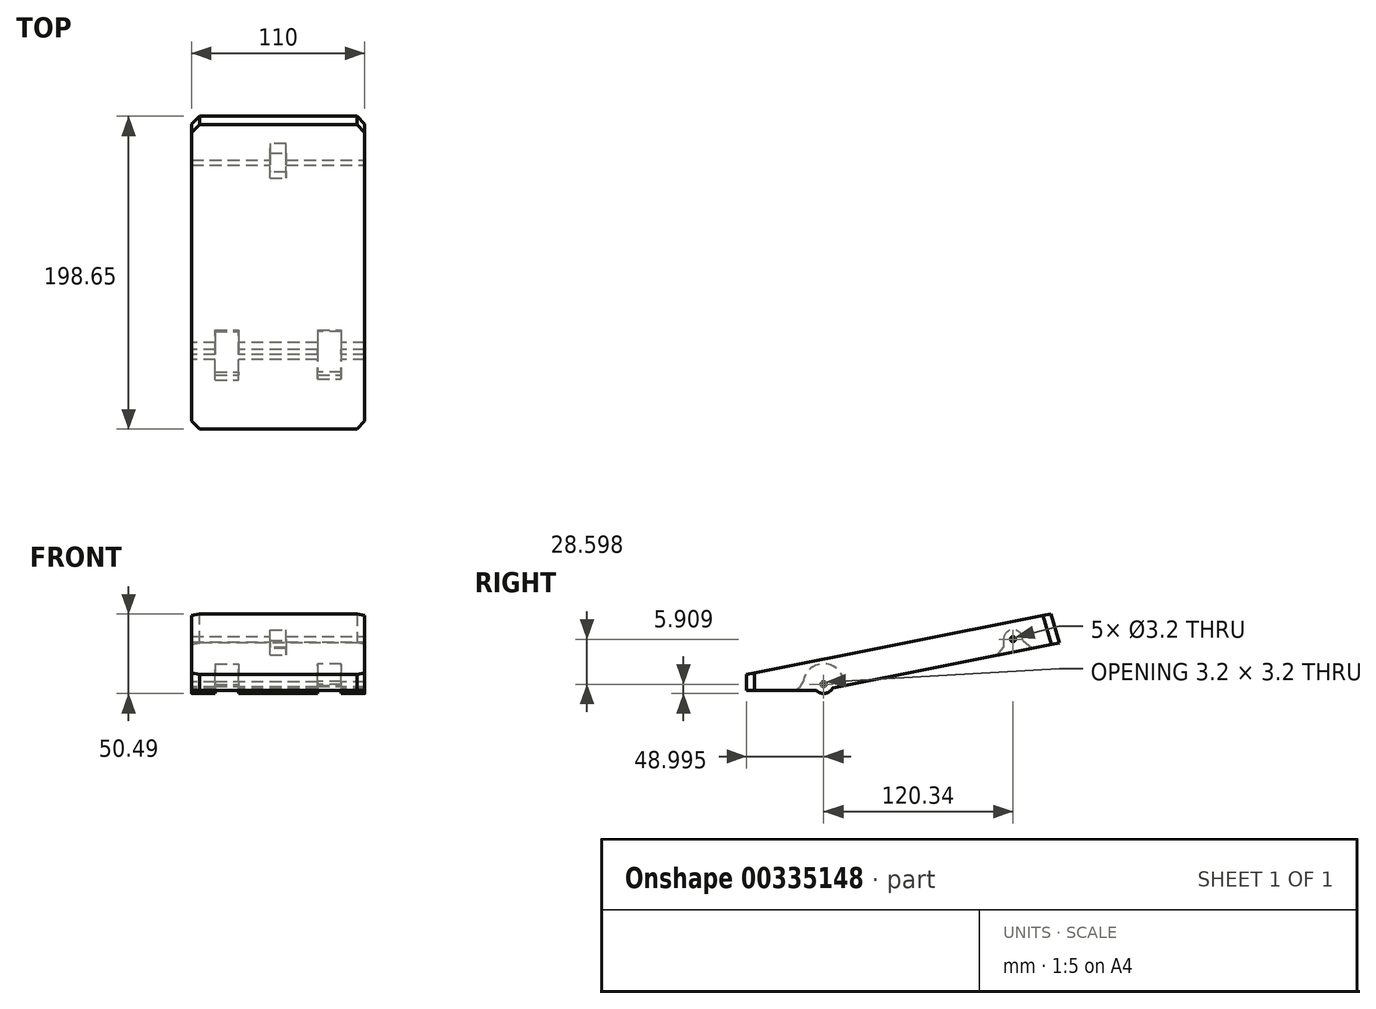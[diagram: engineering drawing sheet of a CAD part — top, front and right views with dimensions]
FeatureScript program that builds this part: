
annotation { "Feature Type Name" : "Feature", "Feature Type Description" : "" }
export const myFeature = defineFeature(function(context is Context, id is Id, definition is map)
    precondition{}
    {
        {
            var Q0;
            Q0=qCreatedBy(makeId("Right.planeOp"),FACE);
            cPlane(context, id + "F0", {"entities" : qUnion([Q0]), "cplaneType" : CPlaneType.OFFSET, "offset" : 55 * mm, "width" : 150 * mm, "height" : 150 * mm});
        }
        {
            var Q0;
            Q0=qCreatedBy(makeId("Right.planeOp"),FACE);
            var sketch = newSketch(context, id + "F1", { "sketchPlane" : qUnion([Q0])});
            skCircle(sketch, "E0.0", {"center": v(-48.56, 3.8) * mm, "radius": 1.6 * mm});
            skArc(sketch, "E1", {"start": v(-53.35, 0) * mm, "mid": v(-47.61, -2.03) * mm, "end": v(-42.71, 1.57) * mm});
            skLineSegment(sketch, "E2", {"start": v(-42.71, 1.57) * mm, "end": v(101.09, 30.13) * mm});
            skLineSegment(sketch, "E3", {"start": v(-97.56, 0) * mm, "end": v(-97.56, 10) * mm});
            skLineSegment(sketch, "E4", {"start": v(-97.56, 10) * mm, "end": v(95.78, 48.39) * mm});
            skLineSegment(sketch, "E5", {"start": v(-53.35, 0) * mm, "end": v(-97.56, 0) * mm});
            skLineSegment(sketch, "E6", {"start": v(95.78, 48.39) * mm, "end": v(101.09, 30.13) * mm});
            skSolve(sketch);
        }
        {
            var Q0;
            Q0 = qSketchRegion(id + "F1", true);
            extrude(context, id + "F2", {"entities" : qUnion([Q0]), "depth" : 110 * mm});
        }
        {
            var Q0;
            Q0=qCreatedBy(makeId("Top.planeOp"),FACE);
            var sketch = newSketch(context, id + "F3", { "sketchPlane" : qUnion([Q0])});
            skLineSegment(sketch, "E7.bottom", {"start": v(15, -55.85) * mm, "end": v(30, -55.85) * mm});
            skLineSegment(sketch, "E7.top", {"start": v(15, -40.85) * mm, "end": v(30, -40.85) * mm});
            skLineSegment(sketch, "E7.left", {"start": v(15, -55.85) * mm, "end": v(15, -40.85) * mm});
            skLineSegment(sketch, "E7.right", {"start": v(30, -55.85) * mm, "end": v(30, -40.85) * mm});
            skLineSegment(sketch, "E8.bottom", {"start": v(80, -55.21) * mm, "end": v(95, -55.21) * mm});
            skLineSegment(sketch, "E8.top", {"start": v(80, -40.21) * mm, "end": v(95, -40.21) * mm});
            skLineSegment(sketch, "E8.left", {"start": v(80, -55.21) * mm, "end": v(80, -40.21) * mm});
            skLineSegment(sketch, "E8.right", {"start": v(95, -55.21) * mm, "end": v(95, -40.21) * mm});
            skSolve(sketch);
        }
        {
            var Q0;
            Q0 = qSketchRegion(id + "F3", true);
            extrude(context, id + "F4", {"entities" : qUnion([Q0]), "operationType" : NewBodyOperationType.REMOVE, "endBound" : BoundingType.SYMMETRIC, "depth" : 21 * mm});
        }
        {
            var Q0;
            Q0=makeQuery(id+"F4.boolean.opBoolean","COPY",FACE,{"derivedFrom":makeQuery(id+"F4.opExtrude","SWEPT_FACE",FACE,{"disambiguationData":[OSD([sQuery(id+"F3.wireOp",EDGE,"E8.left")])]})});
            var sketch = newSketch(context, id + "F5", { "sketchPlane" : qUnion([Q0])});
            skCircle(sketch, "E9.0", {"center": v(-48.56, 3.8) * mm, "radius": 1.6 * mm});
            skArc(sketch, "E10", {"start": v(-35.56, 3.8) * mm, "mid": v(-48.56, 16.8) * mm, "end": v(-61.56, 3.8) * mm});
            skPoint(sketch, "E11.orphan", {"position": v(-97.56, 0) * mm});
            skPoint(sketch, "E12.orphan", {"position": v(-42.71, 1.57) * mm});
            skPoint(sketch, "E13.0.start.orphan", {"position": v(-53.35, 0) * mm});
            skLineSegment(sketch, "E14", {"start": v(-61.56, 3.8) * mm, "end": v(-67.66, -1.5) * mm});
            skLineSegment(sketch, "E15", {"start": v(-67.66, -1.5) * mm, "end": v(-44.57, -13.85) * mm});
            skLineSegment(sketch, "E16", {"start": v(-44.57, -13.85) * mm, "end": v(-28.97, -1.5) * mm});
            skLineSegment(sketch, "E17", {"start": v(-28.97, -1.5) * mm, "end": v(-35.56, 3.8) * mm});
            skPoint(sketch, "E18.end.orphan", {"position": v(0, 3.8) * mm});
            skPoint(sketch, "E19.end.orphan", {"position": v(-61.56, 0) * mm});
            skSolve(sketch);
        }
        {
            var Q0;
            Q0 = qSketchRegion(id + "F5", true);
            var Q1;
            Q1=makeQuery(id+"F4.boolean.opBoolean","INTERSECT",VERTEX,{"derivedFrom":[makeQuery(id+"F2.opExtrude","SWEPT_FACE",FACE,{"disambiguationData":[OSD([sQuery(id+"F1.wireOp",EDGE,"E5")])]}),makeQuery(id+"F4.opExtrude","SWEPT_FACE",FACE,{"disambiguationData":[OSD([sQuery(id+"F3.wireOp",EDGE,"E8.bottom")])]}),makeQuery(id+"F4.opExtrude","SWEPT_FACE",FACE,{"disambiguationData":[OSD([sQuery(id+"F3.wireOp",EDGE,"E8.right")])]})]});
            extrude(context, id + "F6", {"entities" : qUnion([Q0]), "operationType" : NewBodyOperationType.REMOVE, "endBound" : BoundingType.UP_TO_VERTEX, "endBoundEntityVertex" : qUnion([Q1]), "depth" : 25 * mm});
        }
        {
            var Q0;
            Q0=makeQuery(id+"F6.boolean.opBoolean","COPY",EDGE,{"derivedFrom":makeQuery(id+"F6.opExtrude","SWEPT_EDGE",EDGE,{"disambiguationData":[OSD([sQuery(id+"F5.wireOp",EDGE,"E10"),sQuery(id+"F5.wireOp",EDGE,"E14")])]})});
            chamfer(context, id + "F7", {"entities" : qUnion([Q0]), "width" : 5 * mm, "tangentPropagation" : true});
        }
        {
            var Q0;
            Q0=qCreatedBy(id+"F0.planeOp",FACE);
            var sketch = newSketch(context, id + "F8", { "sketchPlane" : qUnion([Q0])});
            skArc(sketch, "E20", {"start": v(77.78, 32.4) * mm, "mid": v(71.78, 38.4) * mm, "end": v(65.78, 32.4) * mm});
            skLineSegment(sketch, "E21", {"start": v(65.78, 32.4) * mm, "end": v(65.78, 22.07) * mm});
            skLineSegment(sketch, "E22", {"start": v(77.78, 32.4) * mm, "end": v(77.78, 22.07) * mm});
            skLineSegment(sketch, "E23", {"start": v(65.78, 22.07) * mm, "end": v(77.78, 22.07) * mm});
            skSolve(sketch);
        }
        {
            var Q0;
            Q0 = qSketchRegion(id + "F8", true);
            extrude(context, id + "F9", {"entities" : qUnion([Q0]), "operationType" : NewBodyOperationType.REMOVE, "endBound" : BoundingType.SYMMETRIC, "oppositeDirection" : true, "depth" : 10 * mm});
        }
        {
            var Q0;
            Q0=makeQuery(id+"F2.opExtrude","CAP_FACE",FACE,{"disambiguationData":[OSD([sQuery(id+"F1.wireOp",EDGE,"E0.0"),sQuery(id+"F1.wireOp",EDGE,"E1"),sQuery(id+"F1.wireOp",EDGE,"E2"),sQuery(id+"F1.wireOp",EDGE,"E3"),sQuery(id+"F1.wireOp",EDGE,"E4"),sQuery(id+"F1.wireOp",EDGE,"E5"),sQuery(id+"F1.wireOp",EDGE,"E6")])],"isStart":false});
            var sketch = newSketch(context, id + "F10", { "sketchPlane" : qUnion([Q0])});
            skCircle(sketch, "E24", {"center": v(71.78, 32.4) * mm, "radius": 1.6 * mm});
            skSolve(sketch);
        }
        {
            var Q0;
            Q0 = qSketchRegion(id + "F10", true);
            extrude(context, id + "F11", {"entities" : qUnion([Q0]), "operationType" : NewBodyOperationType.REMOVE, "endBound" : BoundingType.THROUGH_ALL, "oppositeDirection" : true, "depth" : 25 * mm});
        }
        {
            var Q0;
            Q0=makeQuery(id+"F9.boolean.opBoolean","INTERSECT",EDGE,{"derivedFrom":[makeQuery(id+"F2.opExtrude","SWEPT_FACE",FACE,{"disambiguationData":[OSD([sQuery(id+"F1.wireOp",EDGE,"E2")])]}),makeQuery(id+"F9.opExtrude","SWEPT_FACE",FACE,{"disambiguationData":[OSD([sQuery(id+"F8.wireOp",EDGE,"E22")])]})]});
            chamfer(context, id + "F12", {"entities" : qUnion([Q0]), "width" : 5 * mm, "tangentPropagation" : true});
        }
        {
            var Q0;
            Q0=makeQuery(id+"F9.boolean.opBoolean","INTERSECT",EDGE,{"derivedFrom":[makeQuery(id+"F2.opExtrude","SWEPT_FACE",FACE,{"disambiguationData":[OSD([sQuery(id+"F1.wireOp",EDGE,"E2")])]}),makeQuery(id+"F9.opExtrude","SWEPT_FACE",FACE,{"disambiguationData":[OSD([sQuery(id+"F8.wireOp",EDGE,"E21")])]})]});
            chamfer(context, id + "F13", {"entities" : qUnion([Q0]), "width" : 5 * mm, "tangentPropagation" : true});
        }
        {
            var Q0;
            Q0=makeQuery(id+"F2.opExtrude","CAP_EDGE",EDGE,{"disambiguationData":[OSD([sQuery(id+"F1.wireOp",EDGE,"E6")])],"isStart":true});
            var Q1;
            Q1=makeQuery(id+"F2.opExtrude","CAP_EDGE",EDGE,{"disambiguationData":[OSD([sQuery(id+"F1.wireOp",EDGE,"E6")])],"isStart":false});
            var Q2;
            Q2=makeQuery(id+"FGveSszX63l5Zby_1.opExtrude","SWEPT_EDGE",EDGE,{"disambiguationData":[OSD([sQuery(id+"FY0ePOpRv7rLsL8_1.wireOp",EDGE,"3aef1af1-6b21-466a-8fd8-9d0ddb00b942.2"),sQuery(id+"FY0ePOpRv7rLsL8_1.wireOp",EDGE,"3aef1af1-6b21-466a-8fd8-9d0ddb00b942.3")])]});
            var Q3;
            Q3=makeQuery(id+"F2.opExtrude","CAP_EDGE",EDGE,{"disambiguationData":[OSD([sQuery(id+"F1.wireOp",EDGE,"E3")])],"isStart":false});
            var Q4;
            Q4=makeQuery(id+"F2.opExtrude","CAP_EDGE",EDGE,{"disambiguationData":[OSD([sQuery(id+"F1.wireOp",EDGE,"E3")])],"isStart":true});
            var Q5;
            Q5=makeQuery(id+"FGveSszX63l5Zby_1.opExtrude","SWEPT_EDGE",EDGE,{"disambiguationData":[OSD([sQuery(id+"FY0ePOpRv7rLsL8_1.wireOp",EDGE,"3aef1af1-6b21-466a-8fd8-9d0ddb00b942.0"),sQuery(id+"FY0ePOpRv7rLsL8_1.wireOp",EDGE,"3aef1af1-6b21-466a-8fd8-9d0ddb00b942.3")])]});
            var Q6;
            Q6=makeQuery(id+"FGveSszX63l5Zby_1.opExtrude","SWEPT_EDGE",EDGE,{"disambiguationData":[OSD([sQuery(id+"FY0ePOpRv7rLsL8_1.wireOp",EDGE,"dcda5d86-7792-4639-b30c-51c4dd1823a3.2"),sQuery(id+"FY0ePOpRv7rLsL8_1.wireOp",EDGE,"dcda5d86-7792-4639-b30c-51c4dd1823a3.3")])]});
            var Q7;
            Q7=makeQuery(id+"FGveSszX63l5Zby_1.opExtrude","SWEPT_EDGE",EDGE,{"disambiguationData":[OSD([sQuery(id+"FY0ePOpRv7rLsL8_1.wireOp",EDGE,"dcda5d86-7792-4639-b30c-51c4dd1823a3.0"),sQuery(id+"FY0ePOpRv7rLsL8_1.wireOp",EDGE,"dcda5d86-7792-4639-b30c-51c4dd1823a3.3")])]});
            var Q8;
            Q8=makeQuery(id+"FGveSszX63l5Zby_1.opExtrude","SWEPT_EDGE",EDGE,{"disambiguationData":[OSD([sQuery(id+"FY0ePOpRv7rLsL8_1.wireOp",EDGE,"dcda5d86-7792-4639-b30c-51c4dd1823a3.0"),sQuery(id+"FY0ePOpRv7rLsL8_1.wireOp",EDGE,"dcda5d86-7792-4639-b30c-51c4dd1823a3.1")])]});
            var Q9;
            Q9=makeQuery(id+"FGveSszX63l5Zby_1.opExtrude","SWEPT_EDGE",EDGE,{"disambiguationData":[OSD([sQuery(id+"FY0ePOpRv7rLsL8_1.wireOp",EDGE,"dcda5d86-7792-4639-b30c-51c4dd1823a3.1"),sQuery(id+"FY0ePOpRv7rLsL8_1.wireOp",EDGE,"dcda5d86-7792-4639-b30c-51c4dd1823a3.2")])]});
            chamfer(context, id + "F14", {"entities" : qUnion([Q0, Q1, Q2, Q3, Q4, Q5, Q6, Q7, Q8, Q9]), "width" : 5 * mm, "tangentPropagation" : true});
        }
        {
            var Q0;
            Q0=makeQuery(id+"F4.boolean.opBoolean","COPY",FACE,{"derivedFrom":makeQuery(id+"F4.opExtrude","SWEPT_FACE",FACE,{"disambiguationData":[OSD([sQuery(id+"F3.wireOp",EDGE,"E7.right")])]})});
            var sketch = newSketch(context, id + "F15", { "sketchPlane" : qUnion([Q0])});
            skCircle(sketch, "E25.0", {"center": v(48.56, 3.8) * mm, "radius": 1.6 * mm});
            skArc(sketch, "E26", {"start": v(61.56, 3.8) * mm, "mid": v(48.56, 16.8) * mm, "end": v(35.56, 3.8) * mm});
            skPoint(sketch, "E27.orphan", {"position": v(178.92, 19.57) * mm});
            skPoint(sketch, "E28.0.start.orphan", {"position": v(40.43, -7.24) * mm});
            skPoint(sketch, "E29.0.start.orphan", {"position": v(29.8, -8.82) * mm});
            skLineSegment(sketch, "E30", {"start": v(35.56, 3.8) * mm, "end": v(29.47, -1.5) * mm});
            skLineSegment(sketch, "E31", {"start": v(29.47, -1.5) * mm, "end": v(52.56, -13.85) * mm});
            skLineSegment(sketch, "E32", {"start": v(52.56, -13.85) * mm, "end": v(68.16, -1.5) * mm});
            skLineSegment(sketch, "E33", {"start": v(68.16, -1.5) * mm, "end": v(61.56, 3.8) * mm});
            skPoint(sketch, "E34.end.orphan", {"position": v(21.58, -8.82) * mm});
            skSolve(sketch);
        }
        {
            var Q0;
            Q0 = qSketchRegion(id + "F15", true);
            var Q1;
            Q1=makeQuery(id+"F4.boolean.opBoolean","INTERSECT",VERTEX,{"derivedFrom":[makeQuery(id+"F2.opExtrude","SWEPT_FACE",FACE,{"disambiguationData":[OSD([sQuery(id+"F1.wireOp",EDGE,"E5")])]}),makeQuery(id+"F4.opExtrude","SWEPT_FACE",FACE,{"disambiguationData":[OSD([sQuery(id+"F3.wireOp",EDGE,"E7.bottom")])]}),makeQuery(id+"F4.opExtrude","SWEPT_FACE",FACE,{"disambiguationData":[OSD([sQuery(id+"F3.wireOp",EDGE,"E7.left")])]})]});
            extrude(context, id + "F16", {"entities" : qUnion([Q0]), "operationType" : NewBodyOperationType.REMOVE, "endBound" : BoundingType.UP_TO_VERTEX, "endBoundEntityVertex" : qUnion([Q1]), "depth" : 25 * mm});
        }
        {
            var Q0;
            Q0=makeQuery(id+"F16.boolean.opBoolean","COPY",EDGE,{"derivedFrom":makeQuery(id+"F16.opExtrude","SWEPT_EDGE",EDGE,{"disambiguationData":[OSD([sQuery(id+"F15.wireOp",EDGE,"E26"),sQuery(id+"F15.wireOp",EDGE,"E33")])]})});
            chamfer(context, id + "F17", {"entities" : qUnion([Q0]), "width" : 5 * mm, "tangentPropagation" : true});
        }
    });
